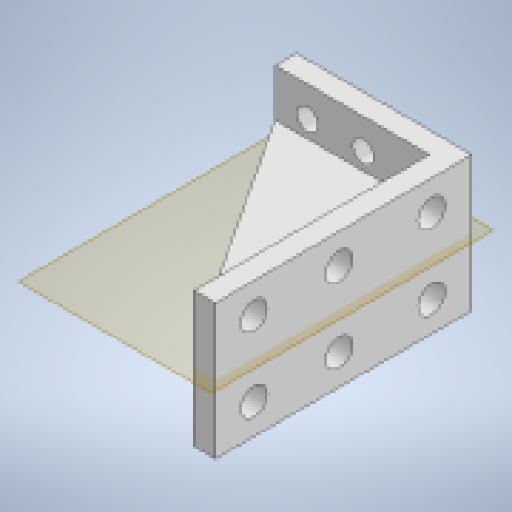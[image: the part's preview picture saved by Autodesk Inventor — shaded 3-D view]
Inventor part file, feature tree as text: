
AUTODESK INVENTOR PART (.ipt)
format: ipt  version: 2025.2 (Build 292293000, 293)  size: 169,984 bytes
history: native  units: mm
features: reference x14, extrude x4, sketch x4, other x4, thread x2, plane x1
ambient origin geometry x8: Origin, YZ Plane, XZ Plane, XY Plane, X Axis, Y Axis, Z Axis, Center Point
bodies: Solid1 (feature_tree)
feature tree (29):
  extrude  "Extrusion1"  Depth=63.5mm TaperAngle=0.0deg
  plane  "Work Plane5"
  extrude  "Extrusion9"  Depth=19.05mm
  extrude  "Extrusion10"  Depth=10.0mm
  extrude  "Extrusion11"  TaperAngle=0.0deg  [1 undecoded]
  sketch  "Sketch1"  dims[d0=10.0mm d1=63.5mm d2=0.0mm]
  reference  "Reference1"
  reference  "Reference2"
  sketch  "Sketch9"  dims[d19=19.05mm d20=0.0mm d21=12.7mm]
  sketch  "Sketch10"  dims[d22=0.0mm d23=0.0mm d24=10.0mm]
  reference  "Reference15"
  reference  "Reference16"
  reference  "Reference17"
  reference  "Reference18"
  reference  "Reference19"
  reference  "Reference20"
  sketch  "Sketch11"  dims[d25=0.0mm d26=0.0mm d28=0.0mm d29=0.0mm d30=0.0mm d31=0.0mm]
  reference  "Reference21"
  reference  "Reference22"
  reference  "Reference23"
  reference  "Reference24"
  reference  "Reference25"
  reference  "Reference26"
  parser-record x1  (decoder bookkeeping rows leaked as tree rows — omitted from the tree; the rows remain in map.json)
  other  "Y_Mount_V2.iam"
  other  "L_Channel:1"
  thread  "Threaded_Rod:2"  [1 undecoded]
  thread  "Threaded_Rod:1"  [1 undecoded]
  other  "3x6_Bar:1"
note: 3 required parameter values undecoded (feature->parameter linkage not recoverable at this tier; creation-order binding heuristic only, values carry confidence <= 0.55)
note: 1 file-system path scrubbed to <path> (originals preserved in map.json)
